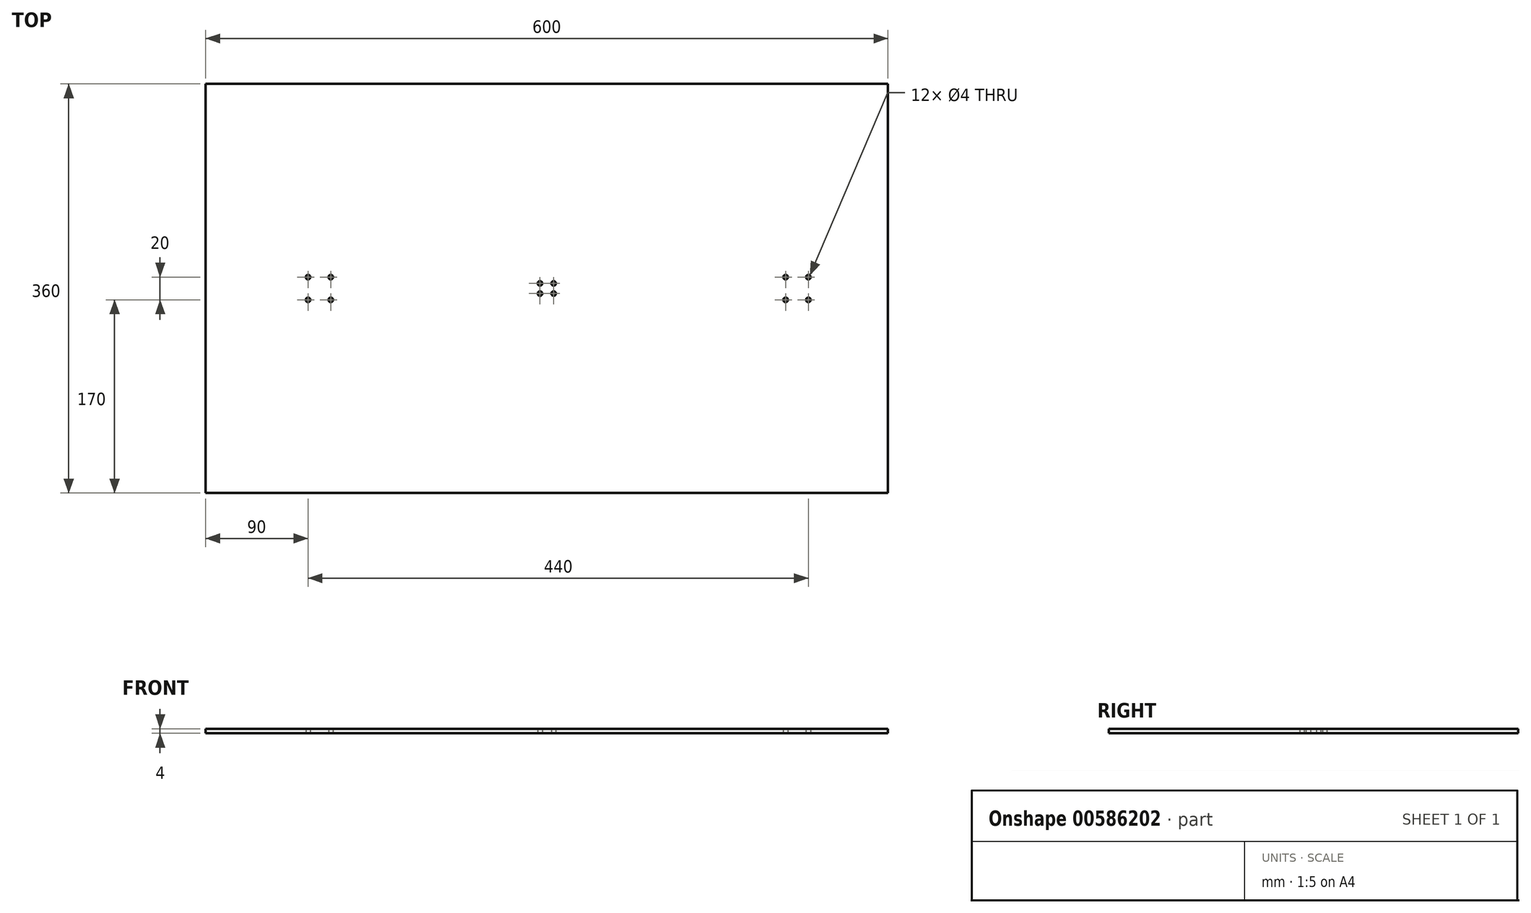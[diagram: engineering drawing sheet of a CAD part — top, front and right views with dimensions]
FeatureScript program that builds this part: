
annotation { "Feature Type Name" : "Feature", "Feature Type Description" : "" }
export const myFeature = defineFeature(function(context is Context, id is Id, definition is map)
    precondition{}
    {
        {
            var Q0;
            Q0=qCreatedBy(makeId("Top.planeOp"),FACE);
            var sketch = newSketch(context, id + "F0", { "sketchPlane" : qUnion([Q0])});
            skPoint(sketch, "E0.middle", {"position": v(0, 0) * mm});
            skPoint(sketch, "E1", {"position": v(6, -4.5) * mm});
            skPoint(sketch, "E2", {"position": v(6, 4.5) * mm});
            skPoint(sketch, "E3", {"position": v(-6, 4.5) * mm});
            skPoint(sketch, "E4", {"position": v(-6, -4.5) * mm});
            skLineSegment(sketch, "E5.bottom", {"start": v(300, -180) * mm, "end": v(-300, -180) * mm});
            skLineSegment(sketch, "E5.top", {"start": v(300, 180) * mm, "end": v(-300, 180) * mm});
            skLineSegment(sketch, "E5.left", {"start": v(300, -180) * mm, "end": v(300, 180) * mm});
            skLineSegment(sketch, "E5.right", {"start": v(-300, -180) * mm, "end": v(-300, 180) * mm});
            skPoint(sketch, "E6", {"position": v(-190, -10) * mm});
            skPoint(sketch, "E7.0.1.0", {"position": v(-190, 10) * mm});
            skPoint(sketch, "E7.1.0.0", {"position": v(-210, -10) * mm});
            skPoint(sketch, "E7.1.1.0", {"position": v(-210, 10) * mm});
            skLineSegment(sketch, "E7.direction1", {"start": v(-190, -10) * mm, "end": v(-210, -10) * mm, "construction": true});
            skLineSegment(sketch, "E7.direction2", {"start": v(-190, -10) * mm, "end": v(-190, 10) * mm, "construction": true});
            skPoint(sketch, "E8.1.0.0", {"position": v(210, -10) * mm});
            skLineSegment(sketch, "E8.direction1", {"start": v(-190, -10) * mm, "end": v(210, -10) * mm, "construction": true});
            skPoint(sketch, "E9.0.1.0", {"position": v(210, 10) * mm});
            skPoint(sketch, "E9.1.0.0", {"position": v(230, -10) * mm});
            skPoint(sketch, "E9.1.1.0", {"position": v(230, 10) * mm});
            skLineSegment(sketch, "E9.direction1", {"start": v(210, -10) * mm, "end": v(230, -10) * mm, "construction": true});
            skLineSegment(sketch, "E9.direction2", {"start": v(210, -10) * mm, "end": v(210, 10) * mm, "construction": true});
            skSolve(sketch);
        }
        {
            var Q0;
            Q0=makeQuery(id+"F0.imprint","IMPRINT",FACE,{"disambiguationData":[TD([[makeQuery(id+"F0.imprint","IMPRINT",EDGE,{"derivedFrom":sQuery(id+"F0.wireOp",EDGE,"E5.bottom")}),-1.0]])]});
            extrude(context, id + "F1", {"entities" : qUnion([Q0]), "depth" : 4 * mm, "offsetDistance" : 25 * mm});
        }
        {
            var Q0;
            Q0=sQuery(id+"F0.wireOp",VERTEX,"E7.1.1.0");
            var Q1;
            Q1=sQuery(id+"F0.wireOp",VERTEX,"E7.0.1.0");
            var Q2;
            Q2=sQuery(id+"F0.wireOp",VERTEX,"E7.1.0.0");
            var Q3;
            Q3=sQuery(id+"F0.wireOp",VERTEX,"E6");
            var Q4;
            Q4=sQuery(id+"F0.wireOp",VERTEX,"E9.1.1.0");
            var Q5;
            Q5=sQuery(id+"F0.wireOp",VERTEX,"E9.0.1.0");
            var Q6;
            Q6=sQuery(id+"F0.wireOp",VERTEX,"E8.1.0.0");
            var Q7;
            Q7=sQuery(id+"F0.wireOp",VERTEX,"E9.1.0.0");
            var Q8;
            Q8=sQuery(id+"F0.wireOp",VERTEX,"E3");
            var Q9;
            Q9=sQuery(id+"F0.wireOp",VERTEX,"E4");
            var Q10;
            Q10=sQuery(id+"F0.wireOp",VERTEX,"E1");
            var Q11;
            Q11=sQuery(id+"F0.wireOp",VERTEX,"E2");
            var Q12;
            Q12=makeQuery(id+"F1.opExtrude","SWEPT_BODY",BODY,{"disambiguationData":[OSD([sQuery(id+"F0.wireOp",EDGE,"E5.bottom"),sQuery(id+"F0.wireOp",EDGE,"E5.top"),sQuery(id+"F0.wireOp",EDGE,"E5.left"),sQuery(id+"F0.wireOp",EDGE,"E5.right")])]});
            hole(context, id + "F2", {"style" : HoleStyle.SIMPLE, "endStyle" : HoleEndStyle.THROUGH, "oppositeDirection" : true, "holeDiameter" : 4 * mm, "majorDiameter" : 5 * mm, "isTappedThrough" : true, "tappedDepth" : 8 * mm, "tapClearance" : 3, "locations" : qUnion([Q0, Q1, Q2, Q3, Q4, Q5, Q6, Q7, Q8, Q9, Q10, Q11]), "scope" : qUnion([Q12])});
        }
    });
